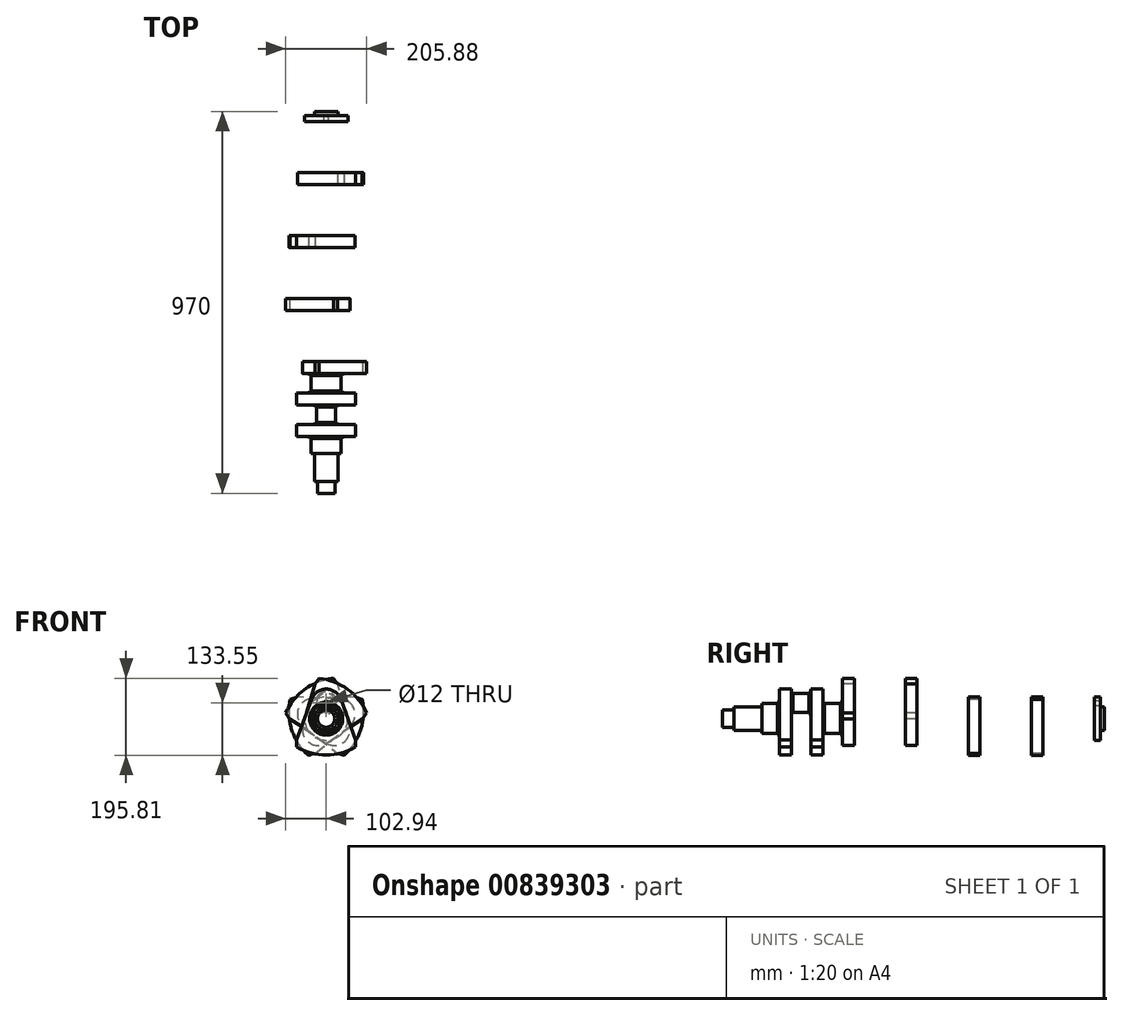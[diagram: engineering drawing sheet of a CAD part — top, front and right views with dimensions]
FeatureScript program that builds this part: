
annotation { "Feature Type Name" : "Feature", "Feature Type Description" : "" }
export const myFeature = defineFeature(function(context is Context, id is Id, definition is map)
    precondition{}
    {
        {
            assignVariable(context, id + "F0", {"name" : "wangen_breite", "anyValue" : 30});
        }
        {
            assignVariable(context, id + "F1", {"name" : "lager_klein_breite", "anyValue" : 50});
        }
        {
            assignVariable(context, id + "F2", {"name" : "lager_gross_breite", "anyValue" : 50});
        }
        {
            assignVariable(context, id + "F3", {"name" : "pleuel_breite", "anyValue" : 2 * getVariable(context, 'wangen_breite') + getVariable(context, 'lager_klein_breite') + getVariable(context, 'lager_gross_breite')});
        }
        {
            var Q0;
            Q0=qCreatedBy(makeId("Front.planeOp"),FACE);
            var sketch = newSketch(context, id + "F4", { "sketchPlane" : qUnion([Q0])});
            skLineSegment(sketch, "E0", {"start": v(-37.59, 48.68) * mm, "end": v(-75, -54.1) * mm});
            skLineSegment(sketch, "E1", {"start": v(-75, -54.1) * mm, "end": v(-75, -71.9) * mm});
            skLineSegment(sketch, "E2", {"start": v(75, -71.9) * mm, "end": v(75, -54.1) * mm});
            skLineSegment(sketch, "E3", {"start": v(75, -54.1) * mm, "end": v(37.59, 48.68) * mm});
            skArc(sketch, "E4", {"start": v(37.59, 48.68) * mm, "mid": v(0, 75) * mm, "end": v(-37.59, 48.68) * mm});
            skArc(sketch, "E5", {"start": v(-75, -71.9) * mm, "mid": v(0, -92) * mm, "end": v(75, -71.9) * mm});
            skSolve(sketch);
        }
        {
            var Q0;
            Q0 = qSketchRegion(id + "F4", true);
            extrude(context, id + "F5", {"entities" : qUnion([Q0]), "oppositeDirection" : true, "depth" : (getVariable(context, 'wangen_breite')) * mm, "offsetDistance" : 25 * mm});
        }
        {
            var Q0;
            Q0=qCreatedBy(makeId("Right.planeOp"),FACE);
            var sketch = newSketch(context, id + "F6", { "sketchPlane" : qUnion([Q0])});
            skLineSegment(sketch, "E6", {"start": v(0, 0) * mm, "end": v(0, 28) * mm});
            skLineSegment(sketch, "E7", {"start": v(0, 28) * mm, "end": v(5, 28) * mm});
            skLineSegment(sketch, "E8", {"start": v(5, 28) * mm, "end": v(5, 24) * mm});
            skLineSegment(sketch, "E9", {"start": v(5, 24) * mm, "end": v(45, 24) * mm});
            skLineSegment(sketch, "E10", {"start": v(45, 24) * mm, "end": v(45, 28) * mm});
            skLineSegment(sketch, "E11", {"start": v(45, 28) * mm, "end": v(50, 28) * mm});
            skLineSegment(sketch, "E12", {"start": v(50, 28) * mm, "end": v(50, 0) * mm});
            skLineSegment(sketch, "E13", {"start": v(50, 0) * mm, "end": v(0, 0) * mm});
            skSolve(sketch);
        }
        {
            var Q0;
            Q0 = qSketchRegion(id + "F6", true);
            var Q1;
            Q1=sQuery(id+"F6.wireOp",EDGE,"E13");
            revolve(context, id + "F7", {"surfaceOperationType" : NewSurfaceOperationType.NEW, "entities" : qUnion([Q0]), "axis" : qUnion([Q1]), "revolveType" : RevolveType.FULL});
        }
        {
            var Q0;
            Q0=qCreatedBy(makeId("Right.planeOp"),FACE);
            var sketch = newSketch(context, id + "F8", { "sketchPlane" : qUnion([Q0])});
            skLineSegment(sketch, "E14", {"start": v(0, 0) * mm, "end": v(0, 42) * mm});
            skLineSegment(sketch, "E15", {"start": v(0, 42) * mm, "end": v(5, 42) * mm});
            skLineSegment(sketch, "E16", {"start": v(5, 42) * mm, "end": v(5, 38) * mm});
            skLineSegment(sketch, "E17", {"start": v(5, 38) * mm, "end": v(45, 38) * mm});
            skLineSegment(sketch, "E18", {"start": v(45, 38) * mm, "end": v(45, 42) * mm});
            skLineSegment(sketch, "E19", {"start": v(45, 42) * mm, "end": v(50, 42) * mm});
            skLineSegment(sketch, "E20", {"start": v(50, 42) * mm, "end": v(50, 0) * mm});
            skLineSegment(sketch, "E21", {"start": v(50, 0) * mm, "end": v(0, 0) * mm});
            skSolve(sketch);
        }
        {
            var Q0;
            Q0 = qSketchRegion(id + "F8", true);
            var Q1;
            Q1=sQuery(id+"F8.wireOp",EDGE,"E21");
            revolve(context, id + "F9", {"surfaceOperationType" : NewSurfaceOperationType.NEW, "entities" : qUnion([Q0]), "axis" : qUnion([Q1]), "revolveType" : RevolveType.FULL});
        }
        {
            var Q0;
            Q0=makeQuery(id+"F5.opExtrude","SWEPT_BODY",BODY,{"disambiguationData":[OSD([sQuery(id+"F4.wireOp",EDGE,"E0"),sQuery(id+"F4.wireOp",EDGE,"E1"),sQuery(id+"F4.wireOp",EDGE,"E2"),sQuery(id+"F4.wireOp",EDGE,"E3"),sQuery(id+"F4.wireOp",EDGE,"E4"),sQuery(id+"F4.wireOp",EDGE,"E5")])]});
            var Q1;
            Q1=qCreatedBy(makeId("Front.planeOp"),FACE);
            transform(context, id + "F10", {"entities" : qUnion([Q0]), "transformType" : TransformType.TRANSLATION_DISTANCE, "transformDirection" : qUnion([Q1]), "distance" : (getVariable(context, 'wangen_breite') + getVariable(context, 'lager_klein_breite')) * mm, "oppositeDirection" : true, "makeCopy" : true});
        }
        {
            var Q0;
            Q0=makeQuery(id+"F7.opRevolve","SWEPT_BODY",BODY,{"disambiguationData":[OSD([sQuery(id+"F6.wireOp",EDGE,"E6"),sQuery(id+"F6.wireOp",EDGE,"E7"),sQuery(id+"F6.wireOp",EDGE,"E8"),sQuery(id+"F6.wireOp",EDGE,"E9"),sQuery(id+"F6.wireOp",EDGE,"E10"),sQuery(id+"F6.wireOp",EDGE,"E11"),sQuery(id+"F6.wireOp",EDGE,"E12"),sQuery(id+"F6.wireOp",EDGE,"E13")])]});
            var Q1;
            Q1=qCreatedBy(makeId("Top.planeOp"),FACE);
            transform(context, id + "F11", {"entities" : qUnion([Q0]), "transformType" : TransformType.TRANSLATION_DISTANCE, "transformDirection" : qUnion([Q1]), "distance" : 40 * mm, "makeCopy" : false});
        }
        {
            var Q0;
            Q0=makeQuery(id+"F7.opRevolve","SWEPT_BODY",BODY,{"disambiguationData":[OSD([sQuery(id+"F6.wireOp",EDGE,"E6"),sQuery(id+"F6.wireOp",EDGE,"E7"),sQuery(id+"F6.wireOp",EDGE,"E8"),sQuery(id+"F6.wireOp",EDGE,"E9"),sQuery(id+"F6.wireOp",EDGE,"E10"),sQuery(id+"F6.wireOp",EDGE,"E11"),sQuery(id+"F6.wireOp",EDGE,"E12"),sQuery(id+"F6.wireOp",EDGE,"E13")])]});
            var Q1;
            Q1=qCreatedBy(makeId("Front.planeOp"),FACE);
            transform(context, id + "F12", {"entities" : qUnion([Q0]), "transformType" : TransformType.TRANSLATION_DISTANCE, "transformDirection" : qUnion([Q1]), "distance" : (getVariable(context, 'wangen_breite')) * mm, "oppositeDirection" : true, "makeCopy" : false});
        }
        {
            var Q0;
            Q0=makeQuery(id+"F9.opRevolve","SWEPT_BODY",BODY,{"disambiguationData":[OSD([sQuery(id+"F8.wireOp",EDGE,"E14"),sQuery(id+"F8.wireOp",EDGE,"E15"),sQuery(id+"F8.wireOp",EDGE,"E16"),sQuery(id+"F8.wireOp",EDGE,"E17"),sQuery(id+"F8.wireOp",EDGE,"E18"),sQuery(id+"F8.wireOp",EDGE,"E19"),sQuery(id+"F8.wireOp",EDGE,"E20"),sQuery(id+"F8.wireOp",EDGE,"E21")])]});
            var Q1;
            Q1=qCreatedBy(makeId("Front.planeOp"),FACE);
            transform(context, id + "F13", {"entities" : qUnion([Q0]), "transformType" : TransformType.TRANSLATION_DISTANCE, "transformDirection" : qUnion([Q1]), "distance" : (2 * getVariable(context, 'wangen_breite') + getVariable(context, 'lager_gross_breite')) * mm, "oppositeDirection" : true, "makeCopy" : false});
        }
        {
            var Q0;
            Q0=makeQuery(id+"F5.opExtrude","SWEPT_BODY",BODY,{"disambiguationData":[OSD([sQuery(id+"F4.wireOp",EDGE,"E0"),sQuery(id+"F4.wireOp",EDGE,"E1"),sQuery(id+"F4.wireOp",EDGE,"E2"),sQuery(id+"F4.wireOp",EDGE,"E3"),sQuery(id+"F4.wireOp",EDGE,"E4"),sQuery(id+"F4.wireOp",EDGE,"E5")])]});
            var Q1;
            Q1=qCreatedBy(makeId("Front.planeOp"),FACE);
            transform(context, id + "F14", {"entities" : qUnion([Q0]), "transformType" : TransformType.TRANSLATION_DISTANCE, "transformDirection" : qUnion([Q1]), "distance" : (getVariable(context, 'pleuel_breite')) * mm, "oppositeDirection" : true, "makeCopy" : true});
        }
        {
            var Q0;
            Q0=makeQuery(id+"F5.opExtrude","SWEPT_BODY",BODY,{"disambiguationData":[OSD([sQuery(id+"F4.wireOp",EDGE,"E0"),sQuery(id+"F4.wireOp",EDGE,"E1"),sQuery(id+"F4.wireOp",EDGE,"E2"),sQuery(id+"F4.wireOp",EDGE,"E3"),sQuery(id+"F4.wireOp",EDGE,"E4"),sQuery(id+"F4.wireOp",EDGE,"E5")])]});
            var Q1;
            Q1=qCreatedBy(makeId("Front.planeOp"),FACE);
            transform(context, id + "F15", {"entities" : qUnion([Q0]), "transformType" : TransformType.TRANSLATION_DISTANCE, "transformDirection" : qUnion([Q1]), "distance" : (2 * getVariable(context, 'pleuel_breite')) * mm, "oppositeDirection" : true, "makeCopy" : true});
        }
        {
            var Q0;
            Q0=makeQuery(id+"F5.opExtrude","SWEPT_BODY",BODY,{"disambiguationData":[OSD([sQuery(id+"F4.wireOp",EDGE,"E0"),sQuery(id+"F4.wireOp",EDGE,"E1"),sQuery(id+"F4.wireOp",EDGE,"E2"),sQuery(id+"F4.wireOp",EDGE,"E3"),sQuery(id+"F4.wireOp",EDGE,"E4"),sQuery(id+"F4.wireOp",EDGE,"E5")])]});
            var Q1;
            Q1=qCreatedBy(makeId("Front.planeOp"),FACE);
            transform(context, id + "F16", {"entities" : qUnion([Q0]), "transformType" : TransformType.TRANSLATION_DISTANCE, "transformDirection" : qUnion([Q1]), "distance" : (3 * getVariable(context, 'pleuel_breite')) * mm, "oppositeDirection" : true, "makeCopy" : true});
        }
        {
            var Q0;
            Q0=makeQuery(id+"F5.opExtrude","SWEPT_BODY",BODY,{"disambiguationData":[OSD([sQuery(id+"F4.wireOp",EDGE,"E0"),sQuery(id+"F4.wireOp",EDGE,"E1"),sQuery(id+"F4.wireOp",EDGE,"E2"),sQuery(id+"F4.wireOp",EDGE,"E3"),sQuery(id+"F4.wireOp",EDGE,"E4"),sQuery(id+"F4.wireOp",EDGE,"E5")])]});
            var Q1;
            Q1=qCreatedBy(makeId("Front.planeOp"),FACE);
            transform(context, id + "F17", {"entities" : qUnion([Q0]), "transformType" : TransformType.TRANSLATION_DISTANCE, "transformDirection" : qUnion([Q1]), "distance" : (4 * getVariable(context, 'pleuel_breite')) * mm, "oppositeDirection" : true, "makeCopy" : true});
        }
        {
            var Q0;
            Q0=makeQuery(id+"F17.opPattern","COPY",BODY,{"derivedFrom":makeQuery(id+"F5.opExtrude","SWEPT_BODY",BODY,{"disambiguationData":[OSD([sQuery(id+"F4.wireOp",EDGE,"E0"),sQuery(id+"F4.wireOp",EDGE,"E1"),sQuery(id+"F4.wireOp",EDGE,"E2"),sQuery(id+"F4.wireOp",EDGE,"E3"),sQuery(id+"F4.wireOp",EDGE,"E4"),sQuery(id+"F4.wireOp",EDGE,"E5")])]}),"instanceName":"1"});
            var Q1;
            Q1=makeQuery(id+"F9.opRevolve","SWEPT_FACE",FACE,{"disambiguationData":[OSD([sQuery(id+"F8.wireOp",EDGE,"E17")])]});
            transform(context, id + "F18", {"entities" : qUnion([Q0]), "transformType" : TransformType.ROTATION, "transformAxis" : qUnion([Q1]), "angle" : 72 * degree, "oppositeDirection" : true, "makeCopy" : false});
        }
        {
            var Q0;
            Q0=makeQuery(id+"F16.opPattern","COPY",BODY,{"derivedFrom":makeQuery(id+"F5.opExtrude","SWEPT_BODY",BODY,{"disambiguationData":[OSD([sQuery(id+"F4.wireOp",EDGE,"E0"),sQuery(id+"F4.wireOp",EDGE,"E1"),sQuery(id+"F4.wireOp",EDGE,"E2"),sQuery(id+"F4.wireOp",EDGE,"E3"),sQuery(id+"F4.wireOp",EDGE,"E4"),sQuery(id+"F4.wireOp",EDGE,"E5")])]}),"instanceName":"1"});
            var Q1;
            Q1=makeQuery(id+"F9.opRevolve","SWEPT_FACE",FACE,{"disambiguationData":[OSD([sQuery(id+"F8.wireOp",EDGE,"E17")])]});
            transform(context, id + "F19", {"entities" : qUnion([Q0]), "transformType" : TransformType.ROTATION, "transformAxis" : qUnion([Q1]), "angle" : 288 * degree, "oppositeDirection" : true, "makeCopy" : false});
        }
        {
            var Q0;
            Q0=makeQuery(id+"F15.opPattern","COPY",BODY,{"derivedFrom":makeQuery(id+"F5.opExtrude","SWEPT_BODY",BODY,{"disambiguationData":[OSD([sQuery(id+"F4.wireOp",EDGE,"E0"),sQuery(id+"F4.wireOp",EDGE,"E1"),sQuery(id+"F4.wireOp",EDGE,"E2"),sQuery(id+"F4.wireOp",EDGE,"E3"),sQuery(id+"F4.wireOp",EDGE,"E4"),sQuery(id+"F4.wireOp",EDGE,"E5")])]}),"instanceName":"1"});
            var Q1;
            Q1=makeQuery(id+"F9.opRevolve","SWEPT_FACE",FACE,{"disambiguationData":[OSD([sQuery(id+"F8.wireOp",EDGE,"E17")])]});
            transform(context, id + "F20", {"entities" : qUnion([Q0]), "transformType" : TransformType.ROTATION, "transformAxis" : qUnion([Q1]), "angle" : 216 * degree, "oppositeDirection" : true, "makeCopy" : false});
        }
        {
            var Q0;
            Q0=makeQuery(id+"F14.opPattern","COPY",BODY,{"derivedFrom":makeQuery(id+"F5.opExtrude","SWEPT_BODY",BODY,{"disambiguationData":[OSD([sQuery(id+"F4.wireOp",EDGE,"E0"),sQuery(id+"F4.wireOp",EDGE,"E1"),sQuery(id+"F4.wireOp",EDGE,"E2"),sQuery(id+"F4.wireOp",EDGE,"E3"),sQuery(id+"F4.wireOp",EDGE,"E4"),sQuery(id+"F4.wireOp",EDGE,"E5")])]}),"instanceName":"1"});
            var Q1;
            Q1=makeQuery(id+"F9.opRevolve","SWEPT_FACE",FACE,{"disambiguationData":[OSD([sQuery(id+"F8.wireOp",EDGE,"E17")])]});
            transform(context, id + "F21", {"entities" : qUnion([Q0]), "transformType" : TransformType.ROTATION, "transformAxis" : qUnion([Q1]), "angle" : 144 * degree, "oppositeDirection" : true, "makeCopy" : false});
        }
        {
            var Q0;
            Q0=qCreatedBy(makeId("Right.planeOp"),FACE);
            var sketch = newSketch(context, id + "F22", { "sketchPlane" : qUnion([Q0])});
            skLineSegment(sketch, "E22", {"start": v(0, 0) * mm, "end": v(-145, 0) * mm});
            skLineSegment(sketch, "E23", {"start": v(-145, 0) * mm, "end": v(-145, 22) * mm});
            skLineSegment(sketch, "E24", {"start": v(-145, 22) * mm, "end": v(-115, 22) * mm});
            skLineSegment(sketch, "E25", {"start": v(-115, 22) * mm, "end": v(-115, 30) * mm});
            skLineSegment(sketch, "E26", {"start": v(-115, 30) * mm, "end": v(-44, 30) * mm});
            skLineSegment(sketch, "E27", {"start": v(-44, 30) * mm, "end": v(-44, 38) * mm});
            skLineSegment(sketch, "E28", {"start": v(-44, 38) * mm, "end": v(-5, 38) * mm});
            skLineSegment(sketch, "E29", {"start": v(-5, 38) * mm, "end": v(-5, 42) * mm});
            skLineSegment(sketch, "E30", {"start": v(-5, 42) * mm, "end": v(0, 42) * mm});
            skLineSegment(sketch, "E31", {"start": v(0, 42) * mm, "end": v(0, 0) * mm});
            skSolve(sketch);
        }
        {
            var Q0;
            Q0 = qSketchRegion(id + "F22", true);
            var Q1;
            Q1=sQuery(id+"F22.wireOp",EDGE,"E22");
            revolve(context, id + "F23", {"surfaceOperationType" : NewSurfaceOperationType.NEW, "entities" : qUnion([Q0]), "axis" : qUnion([Q1]), "revolveType" : RevolveType.FULL});
        }
        {
            var Q0;
            Q0=qCreatedBy(makeId("Right.planeOp"),FACE);
            var sketch = newSketch(context, id + "F24", { "sketchPlane" : qUnion([Q0])});
            skLineSegment(sketch, "E32", {"start": v(0, 0) * mm, "end": v(0, 55) * mm});
            skLineSegment(sketch, "E33", {"start": v(0, 55) * mm, "end": v(15, 55) * mm});
            skLineSegment(sketch, "E34", {"start": v(15, 55) * mm, "end": v(15, 30) * mm});
            skLineSegment(sketch, "E35", {"start": v(15, 30) * mm, "end": v(25, 30) * mm});
            skLineSegment(sketch, "E36", {"start": v(25, 30) * mm, "end": v(25, 0) * mm});
            skLineSegment(sketch, "E37", {"start": v(25, 0) * mm, "end": v(0, 0) * mm});
            skSolve(sketch);
        }
        {
            var Q0;
            Q0 = qSketchRegion(id + "F24", true);
            var Q1;
            Q1=sQuery(id+"F24.wireOp",EDGE,"E37");
            revolve(context, id + "F25", {"surfaceOperationType" : NewSurfaceOperationType.NEW, "entities" : qUnion([Q0]), "axis" : qUnion([Q1]), "revolveType" : RevolveType.FULL});
        }
        {
            var Q0;
            Q0=makeQuery(id+"F25.opRevolve","SWEPT_FACE",FACE,{"disambiguationData":[OSD([sQuery(id+"F24.wireOp",EDGE,"E34")])]});
            var sketch = newSketch(context, id + "F26", { "sketchPlane" : qUnion([Q0])});
            skPoint(sketch, "E38", {"position": v(0, 40) * mm});
            skSolve(sketch);
        }
        {
            var Q0;
            Q0=sQuery(id+"F26.wireOp",VERTEX,"E38");
            var Q1;
            Q1=makeQuery(id+"F25.opRevolve","SWEPT_BODY",BODY,{"disambiguationData":[OSD([sQuery(id+"F24.wireOp",EDGE,"E32"),sQuery(id+"F24.wireOp",EDGE,"E33"),sQuery(id+"F24.wireOp",EDGE,"E34"),sQuery(id+"F24.wireOp",EDGE,"E35"),sQuery(id+"F24.wireOp",EDGE,"E36"),sQuery(id+"F24.wireOp",EDGE,"E37")])]});
            hole(context, id + "F27", {"style" : HoleStyle.SIMPLE, "endStyle" : HoleEndStyle.THROUGH, "holeDiameter" : 12 * mm, "majorDiameter" : 5 * mm, "isTappedThrough" : true, "tappedDepth" : 12 * mm, "tapClearance" : 3, "locations" : qUnion([Q0]), "scope" : qUnion([Q1])});
        }
        {
            var Q0;
            Q0=makeQuery(id+"F25.opRevolve","SWEPT_BODY",BODY,{"disambiguationData":[OSD([sQuery(id+"F24.wireOp",EDGE,"E32"),sQuery(id+"F24.wireOp",EDGE,"E33"),sQuery(id+"F24.wireOp",EDGE,"E34"),sQuery(id+"F24.wireOp",EDGE,"E35"),sQuery(id+"F24.wireOp",EDGE,"E36"),sQuery(id+"F24.wireOp",EDGE,"E37")])]});
            var Q1;
            Q1=qCreatedBy(makeId("Front.planeOp"),FACE);
            transform(context, id + "F28", {"entities" : qUnion([Q0]), "transformType" : TransformType.TRANSLATION_DISTANCE, "transformDirection" : qUnion([Q1]), "distance" : (5 * getVariable(context, 'pleuel_breite')) * mm, "oppositeDirection" : true, "makeCopy" : false});
        }
    });
